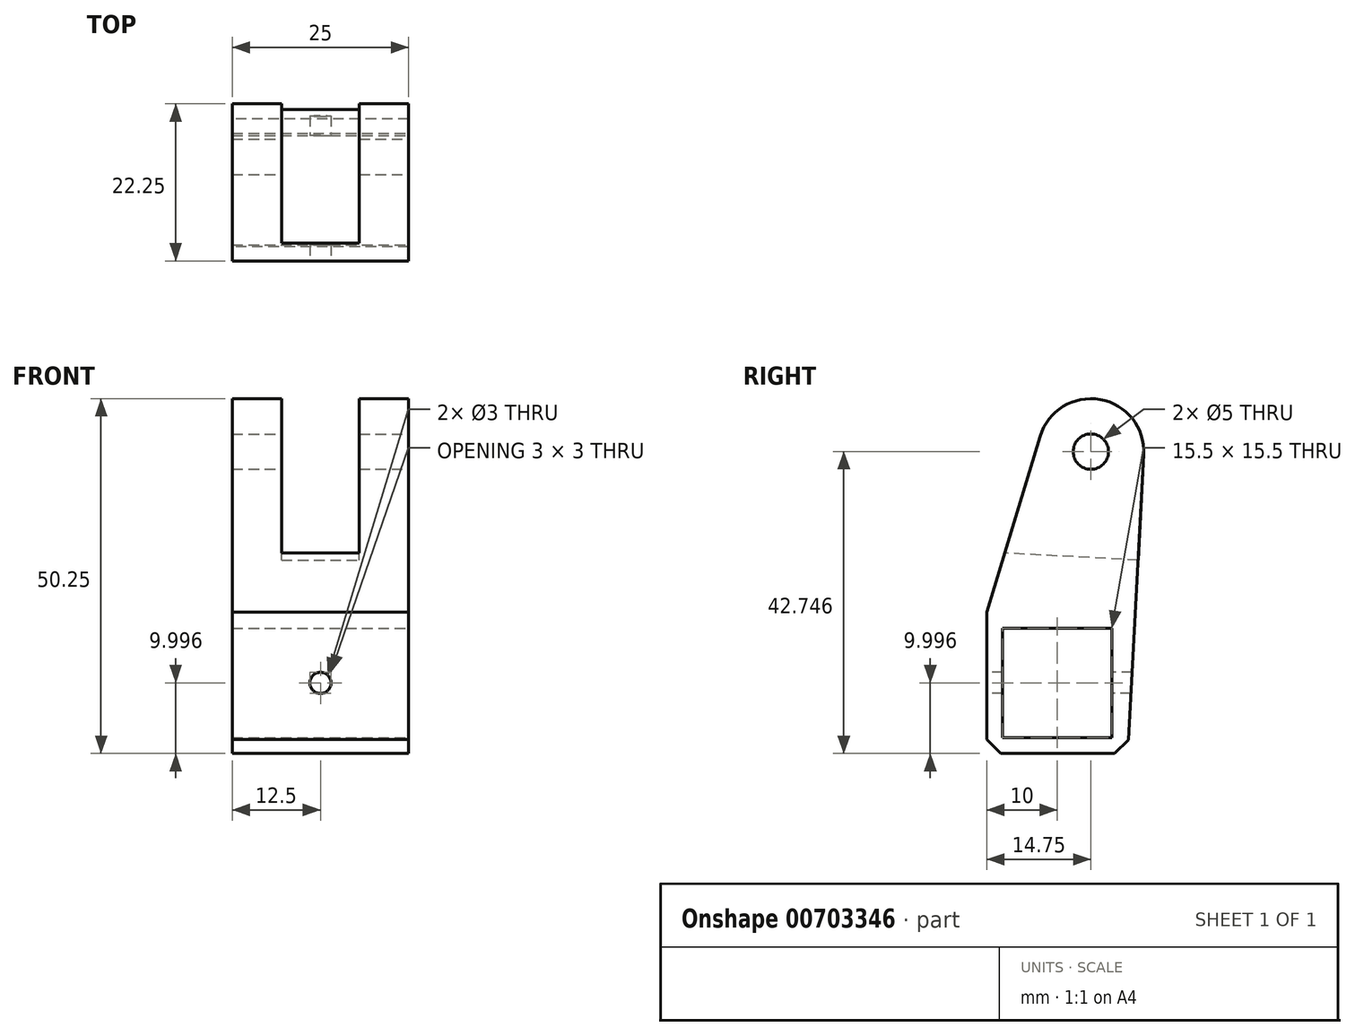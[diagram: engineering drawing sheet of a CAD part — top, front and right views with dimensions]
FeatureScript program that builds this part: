
annotation { "Feature Type Name" : "Feature", "Feature Type Description" : "" }
export const myFeature = defineFeature(function(context is Context, id is Id, definition is map)
    precondition{}
    {
        {
            var Q0;
            Q0=qCreatedBy(makeId("Right.planeOp"),FACE);
            var sketch = newSketch(context, id + "F0", { "sketchPlane" : qUnion([Q0])});
            skLineSegment(sketch, "E0.bottom", {"start": v(-40.3, 12.2) * mm, "end": v(-55.8, 12.2) * mm});
            skLineSegment(sketch, "E0.top", {"start": v(-40.3, 27.7) * mm, "end": v(-55.8, 27.7) * mm});
            skLineSegment(sketch, "E0.left", {"start": v(-40.3, 12.2) * mm, "end": v(-40.3, 27.7) * mm});
            skLineSegment(sketch, "E0.right", {"start": v(-55.8, 12.2) * mm, "end": v(-55.8, 27.7) * mm});
            skPoint(sketch, "E0.middle", {"position": v(-48.06, 19.95) * mm});
            skLineSegment(sketch, "E1.bottom", {"start": v(-58.06, 29.95) * mm, "end": v(-38.06, 29.95) * mm});
            skLineSegment(sketch, "E1.top", {"start": v(-58.06, 9.95) * mm, "end": v(-38.06, 9.95) * mm});
            skLineSegment(sketch, "E1.left", {"start": v(-58.06, 29.95) * mm, "end": v(-58.06, 9.95) * mm});
            skLineSegment(sketch, "E1.right", {"start": v(-38.06, 29.95) * mm, "end": v(-38.06, 9.95) * mm});
            skCircle(sketch, "E2", {"center": v(-43.3, 52.7) * mm, "radius": 2.5 * mm});
            skCircle(sketch, "E3", {"center": v(-43.3, 52.7) * mm, "radius": 7.5 * mm});
            skLineSegment(sketch, "E4", {"start": v(-58.06, 29.95) * mm, "end": v(-50.49, 54.88) * mm});
            skLineSegment(sketch, "E5", {"start": v(-38.06, 9.95) * mm, "end": v(-35.82, 52.3) * mm});
            skLineSegment(sketch, "E6", {"start": v(-36.61, 37.32) * mm, "end": v(-55.52, 38.32) * mm});
            skSolve(sketch);
        }
        {
            var Q0;
            Q0=makeQuery(id+"F0.imprint","IMPRINT",FACE,{"disambiguationData":[TD([[makeQuery(id+"F0.imprint","IMPRINT",EDGE,{"derivedFrom":sQuery(id+"F0.wireOp",EDGE,"E1.bottom")}),1.0]])]});
            var Q1;
            Q1=makeQuery(id+"F0.imprint","IMPRINT",FACE,{"disambiguationData":[TD([[makeQuery(id+"F0.imprint","IMPRINT",EDGE,{"derivedFrom":sQuery(id+"F0.wireOp",EDGE,"E2")}),-1.0]])]});
            var Q2;
            Q2=makeQuery(id+"F0.imprint","IMPRINT",FACE,{"disambiguationData":[TD([[makeQuery(id+"F0.imprint","IMPRINT",EDGE,{"derivedFrom":sQuery(id+"F0.wireOp",EDGE,"E0.bottom")}),1.0]])]});
            var Q3;
            {var subQ5=sQuery(id+"F0.wireOp",EDGE,"E6");Q3=makeQuery(id+"F0.imprint","IMPRINT",FACE,{"disambiguationData":[TD([[makeQuery(id+"F0.imprint","IMPRINT",EDGE,{"derivedFrom":subQ5}),-1.0]])]});}
            extrude(context, id + "F1", {"entities" : qUnion([Q0, Q1, Q2, Q3]), "oppositeDirection" : true, "depth" : 25 * mm, "offsetDistance" : 25 * mm});
        }
        {
            var Q0;
            {var subQ5=sQuery(id+"F0.wireOp",EDGE,"E6");Q0=makeQuery(id+"F0.imprint","IMPRINT",FACE,{"disambiguationData":[TD([[makeQuery(id+"F0.imprint","IMPRINT",EDGE,{"derivedFrom":subQ5}),-1.0]])]});}
            var Q1;
            Q1=makeQuery(id+"F0.imprint","IMPRINT",FACE,{"disambiguationData":[TD([[makeQuery(id+"F0.imprint","IMPRINT",EDGE,{"derivedFrom":sQuery(id+"F0.wireOp",EDGE,"E2")}),-1.0]])]});
            extrude(context, id + "F2", {"entities" : qUnion([Q0, Q1]), "operationType" : NewBodyOperationType.REMOVE, "oppositeDirection" : true, "depth" : (25 - 7) * mm, "offsetDistance" : 25 * mm, "hasSecondDirection" : true, "secondDirectionOppositeDirection" : true, "secondDirectionDepth" : 7 * mm});
        }
        {
            var Q0;
            Q0=makeQuery(id+"F1.opExtrude","SWEPT_FACE",FACE,{"disambiguationData":[OSD([sQuery(id+"F0.wireOp",EDGE,"E1.left")])]});
            var sketch = newSketch(context, id + "F3", { "sketchPlane" : qUnion([Q0])});
            skLineSegment(sketch, "E7", {"start": v(-25, 29.95) * mm, "end": v(0, 9.95) * mm, "construction": true});
            skLineSegment(sketch, "E8", {"start": v(0, 9.95) * mm, "end": v(0, 29.95) * mm, "construction": true});
            skLineSegment(sketch, "E9", {"start": v(0, 29.95) * mm, "end": v(-25, 9.95) * mm, "construction": true});
            skCircle(sketch, "E10", {"center": v(-12.5, 19.95) * mm, "radius": 1.5 * mm});
            skSolve(sketch);
        }
        {
            var Q0;
            Q0=makeQuery(id+"F3.imprint","IMPRINT",FACE,{"disambiguationData":[TD([[makeQuery(id+"F3.imprint","IMPRINT",EDGE,{"derivedFrom":sQuery(id+"F3.wireOp",EDGE,"E10")}),1.0]])]});
            extrude(context, id + "F4", {"entities" : qUnion([Q0]), "operationType" : NewBodyOperationType.REMOVE, "oppositeDirection" : true, "depth" : 25 * mm, "offsetDistance" : 25 * mm});
        }
        {
            var Q0;
            Q0=makeQuery(id+"F1.opExtrude","SWEPT_EDGE",EDGE,{"disambiguationData":[OSD([sQuery(id+"F0.wireOp",EDGE,"E1.top"),sQuery(id+"F0.wireOp",EDGE,"E1.left")])]});
            var Q1;
            Q1=makeQuery(id+"F1.opExtrude","SWEPT_EDGE",EDGE,{"disambiguationData":[OSD([sQuery(id+"F0.wireOp",EDGE,"E1.top"),sQuery(id+"F0.wireOp",EDGE,"E1.right"),sQuery(id+"F0.wireOp",EDGE,"E5")])]});
            chamfer(context, id + "F5", {"entities" : qUnion([Q0, Q1]), "width" : 2 * mm, "tangentPropagation" : true});
        }
    });
